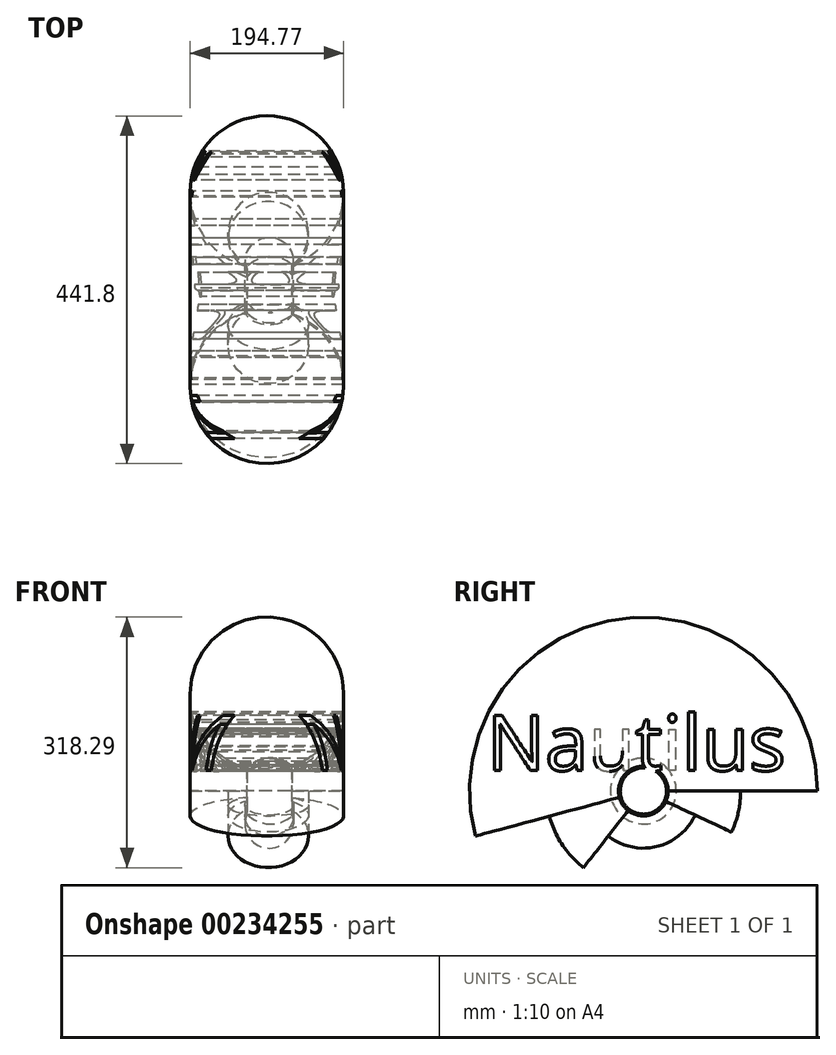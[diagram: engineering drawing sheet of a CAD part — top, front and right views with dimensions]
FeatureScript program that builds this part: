
annotation { "Feature Type Name" : "Feature", "Feature Type Description" : "" }
export const myFeature = defineFeature(function(context is Context, id is Id, definition is map)
    precondition{}
    {
        {
            var Q0;
            Q0=qCreatedBy(makeId("Top.planeOp"),FACE);
            var sketch = newSketch(context, id + "F0", { "sketchPlane" : qUnion([Q0])});
            skArc(sketch, "E0", {"start": v(219.37, 32.07) * mm, "mid": v(183.6, 221.33) * mm, "end": v(162.13, 29.93) * mm});
            skArc(sketch, "E1", {"start": v(219.37, 32.07) * mm, "mid": v(187.26, 124.01) * mm, "end": v(162.13, 29.93) * mm});
            skArc(sketch, "E2", {"start": v(219.37, 32.07) * mm, "mid": v(189.17, 73.1) * mm, "end": v(162.13, 29.93) * mm});
            skArc(sketch, "E3", {"start": v(219.37, 32.07) * mm, "mid": v(190.32, 42.32) * mm, "end": v(162.13, 29.93) * mm});
            skPoint(sketch, "E4", {"position": v(183.6, 221.33) * mm});
            skText(sketch, "E5", { "text": "ABUSH\n", "fontName": "OpenSans-Regular.ttf"});
            skLineSegment(sketch, "E6.bottom", {"start": v(374.99, 124.94) * mm, "end": v(316.35, 124.94) * mm});
            skLineSegment(sketch, "E6.top", {"start": v(355.94, 68.9) * mm, "end": v(316.35, 68.9) * mm});
            skLineSegment(sketch, "E6.left", {"start": v(381.34, 118.6) * mm, "end": v(381.34, 94.3) * mm});
            skLineSegment(sketch, "E6.right", {"start": v(316.35, 124.94) * mm, "end": v(316.35, 68.9) * mm});
            skPoint(sketch, "E7.visualSharp", {"position": v(381.34, 124.94) * mm});
            skArc(sketch, "E7.filletArc", {"start": v(381.34, 118.6) * mm, "mid": v(379.48, 123.08) * mm, "end": v(374.99, 124.94) * mm});
            skPoint(sketch, "E8.visualSharp", {"position": v(381.34, 68.9) * mm});
            skArc(sketch, "E8.filletArc", {"start": v(355.94, 68.9) * mm, "mid": v(373.9, 76.34) * mm, "end": v(381.34, 94.3) * mm});
            skLineSegment(sketch, "E9", {"start": v(191.9, 0.5) * mm, "end": v(102.74, 0.5) * mm, "construction": true});
            skLineSegment(sketch, "E10", {"start": v(102.74, 0.5) * mm, "end": v(246.9, 0.5) * mm, "construction": true});
            const initialGuessF0  = {"E5": [0.39323, 0.16515, 1, 0, 0.06654]};
            skSetInitialGuess(sketch, initialGuessF0);
            skSolve(sketch);
        }
        {
            var Q0;
            Q0=makeQuery(id+"F0.imprint","IMPRINT",FACE,{"disambiguationData":[TD([[makeQuery(id+"F0.imprint","IMPRINT",EDGE,{"derivedFrom":sQuery(id+"F0.wireOp",EDGE,"E2")}),1.0]])]});
            var Q1;
            Q1=sQuery(id+"F0.wireOp",EDGE,"E10");
            revolve(context, id + "F1", {"entities" : qUnion([Q0]), "axis" : qUnion([Q1]), "revolveType" : RevolveType.FULL});
        }
        {
            var Q0;
            Q0=makeQuery(id+"F0.imprint","IMPRINT",FACE,{"disambiguationData":[TD([[makeQuery(id+"F0.imprint","IMPRINT",EDGE,{"derivedFrom":sQuery(id+"F0.wireOp",EDGE,"E1")}),1.0]])]});
            var Q1;
            Q1=sQuery(id+"F0.wireOp",EDGE,"E10");
            revolve(context, id + "F2", {"operationType" : NewBodyOperationType.ADD, "entities" : qUnion([Q0]), "axis" : qUnion([Q1]), "revolveType" : RevolveType.TWO_DIRECTIONS, "oppositeDirection" : true, "angle" : 25 * degree, "angleBack" : 127.98 * degree});
        }
        {
            var Q0;
            Q0=makeQuery(id+"F0.imprint","IMPRINT",FACE,{"disambiguationData":[TD([[makeQuery(id+"F0.imprint","IMPRINT",EDGE,{"derivedFrom":sQuery(id+"F0.wireOp",EDGE,"E0")}),1.0]])]});
            var Q1;
            Q1=sQuery(id+"F0.wireOp",EDGE,"E10");
            revolve(context, id + "F3", {"operationType" : NewBodyOperationType.ADD, "entities" : qUnion([Q0]), "axis" : qUnion([Q1]), "revolveType" : RevolveType.ONE_DIRECTION, "angle" : 195 * degree});
        }
        {
            var Q0;
            Q0=qCreatedBy(makeId("Right.planeOp"),FACE);
            var sketch = newSketch(context, id + "F4", { "sketchPlane" : qUnion([Q0])});
            skText(sketch, "E11", { "text": "Nautilus", "fontName": "OpenSans-Regular.ttf"});
            const initialGuessF4  = {"E11": [-0.198, 0.02593, 1, 0, 0.07048]};
            skSetInitialGuess(sketch, initialGuessF4);
            skSolve(sketch);
        }
        {
            var Q0;
            Q0 = qSketchRegion(id + "F4", true);
            extrude(context, id + "F5", {"entities" : qUnion([Q0]), "operationType" : NewBodyOperationType.REMOVE, "depth" : 317.5 * mm});
        }
    });
